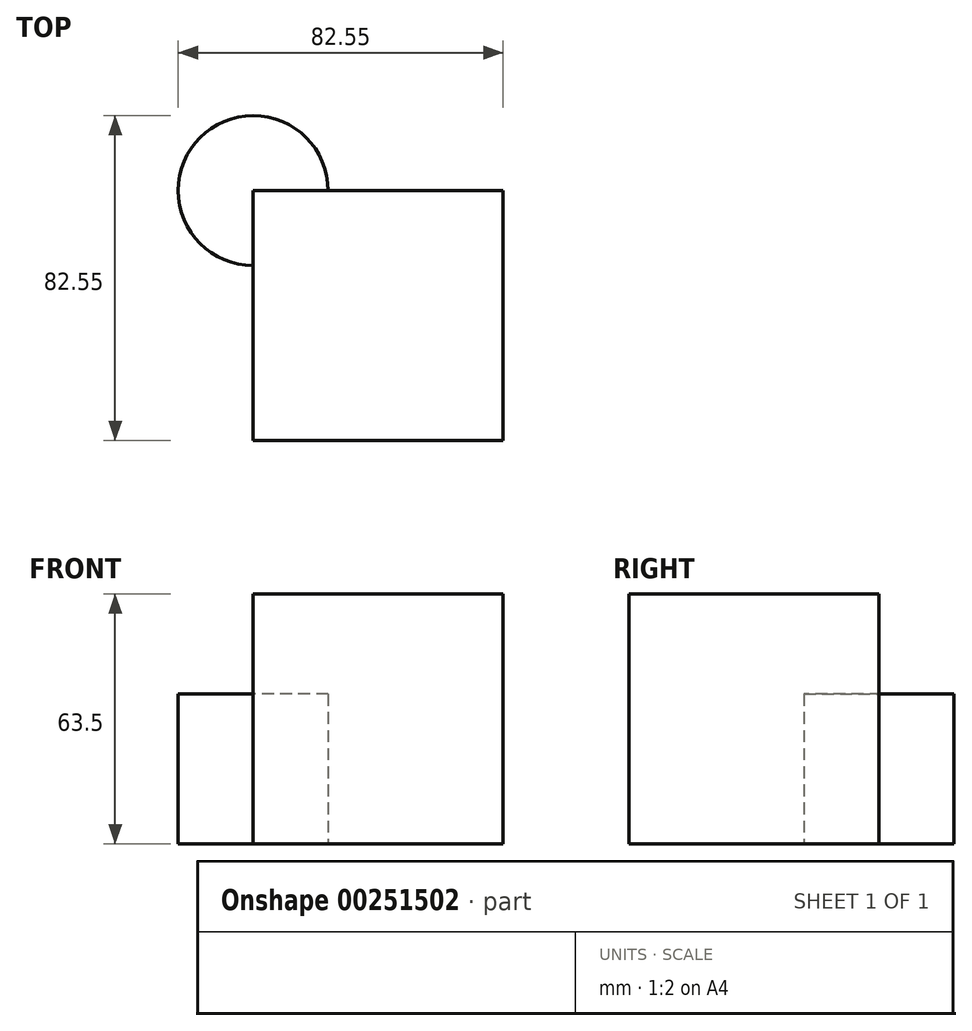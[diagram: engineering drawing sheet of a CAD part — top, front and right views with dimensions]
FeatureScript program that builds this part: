
annotation { "Feature Type Name" : "Feature", "Feature Type Description" : "" }
export const myFeature = defineFeature(function(context is Context, id is Id, definition is map)
    precondition{}
    {
        {
            var Q0;
            Q0=qCreatedBy(makeId("Front.planeOp"),FACE);
            var sketch = newSketch(context, id + "F0", { "sketchPlane" : qUnion([Q0])});
            skLineSegment(sketch, "E0.bottom", {"start": v(0, 0) * mm, "end": v(63.5, 0) * mm});
            skLineSegment(sketch, "E0.top", {"start": v(0, 63.5) * mm, "end": v(63.5, 63.5) * mm});
            skLineSegment(sketch, "E0.left", {"start": v(0, 0) * mm, "end": v(0, 63.5) * mm});
            skLineSegment(sketch, "E0.right", {"start": v(63.5, 0) * mm, "end": v(63.5, 63.5) * mm});
            skSolve(sketch);
        }
        {
            var Q0;
            Q0 = qSketchRegion(id + "F0", true);
            extrude(context, id + "F1", {"entities" : qUnion([Q0]), "depth" : 63.5 * mm});
        }
        {
            var Q0;
            Q0=qCreatedBy(makeId("Top.planeOp"),FACE);
            var sketch = newSketch(context, id + "F2", { "sketchPlane" : qUnion([Q0])});
            skCircle(sketch, "E1", {"center": v(0, 0) * mm, "radius": 19.05 * mm});
            skSolve(sketch);
        }
        {
            var Q0;
            Q0 = qSketchRegion(id + "F2", true);
            extrude(context, id + "F3", {"entities" : qUnion([Q0]), "operationType" : NewBodyOperationType.ADD, "depth" : 38.1 * mm});
        }
        {
            var Q0;
            Q0=qCreatedBy(makeId("Top.planeOp"),FACE);
            var sketch = newSketch(context, id + "F4", { "sketchPlane" : qUnion([Q0])});
            skCircle(sketch, "E2", {"center": v(0, 0) * mm, "radius": 19.05 * mm});
            skSolve(sketch);
        }
        {
            var Q0;
            Q0 = qSketchRegion(id + "F4", true);
            extrude(context, id + "F5", {"entities" : qUnion([Q0]), "operationType" : NewBodyOperationType.ADD, "depth" : 38.1 * mm});
        }
    });
